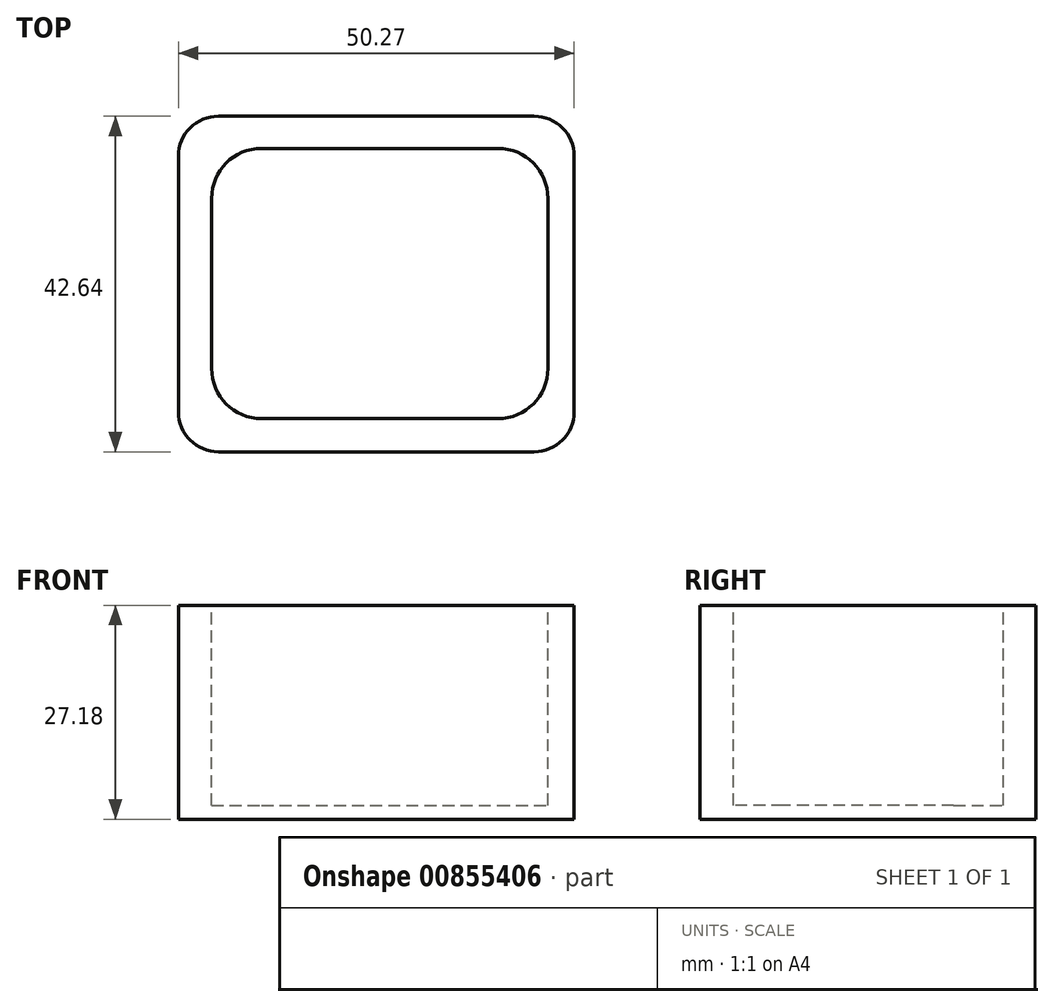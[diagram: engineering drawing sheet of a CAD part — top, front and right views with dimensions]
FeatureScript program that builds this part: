
annotation { "Feature Type Name" : "Feature", "Feature Type Description" : "" }
export const myFeature = defineFeature(function(context is Context, id is Id, definition is map)
    precondition{}
    {
        {
            var Q0;
            Q0=qCreatedBy(makeId("Top.planeOp"),FACE);
            var sketch = newSketch(context, id + "F0", { "sketchPlane" : qUnion([Q0])});
            skLineSegment(sketch, "E0.bottom", {"start": v(-56.09, -24.44) * mm, "end": v(-5.82, -24.44) * mm});
            skLineSegment(sketch, "E0.top", {"start": v(-56.09, -67.08) * mm, "end": v(-5.82, -67.08) * mm});
            skLineSegment(sketch, "E0.left", {"start": v(-56.09, -24.44) * mm, "end": v(-56.09, -67.08) * mm});
            skLineSegment(sketch, "E0.right", {"start": v(-5.82, -24.44) * mm, "end": v(-5.82, -67.08) * mm});
            skSolve(sketch);
        }
        {
            var Q0;
            Q0=makeQuery(id+"F0.imprint","IMPRINT",FACE,{"disambiguationData":[TD([[makeQuery(id+"F0.imprint","IMPRINT",EDGE,{"derivedFrom":sQuery(id+"F0.wireOp",EDGE,"E0.bottom")}),-1.0]])]});
            extrude(context, id + "F1", {"entities" : qUnion([Q0]), "depth" : 27.18 * mm, "offsetDistance" : 25.4 * mm});
        }
        {
            var Q0;
            Q0=makeQuery(id+"F1.opExtrude","CAP_FACE",FACE,{"disambiguationData":[OSD([sQuery(id+"F0.wireOp",EDGE,"E0.bottom"),sQuery(id+"F0.wireOp",EDGE,"E0.top"),sQuery(id+"F0.wireOp",EDGE,"E0.left"),sQuery(id+"F0.wireOp",EDGE,"E0.right")])],"isStart":false});
            var sketch = newSketch(context, id + "F2", { "sketchPlane" : qUnion([Q0])});
            skLineSegment(sketch, "E1.bottom", {"start": v(-45.52, -28.53) * mm, "end": v(-15.5, -28.53) * mm});
            skLineSegment(sketch, "E1.top", {"start": v(-45.52, -62.85) * mm, "end": v(-15.5, -62.85) * mm});
            skLineSegment(sketch, "E1.left", {"start": v(-51.87, -34.88) * mm, "end": v(-51.87, -56.5) * mm});
            skLineSegment(sketch, "E1.right", {"start": v(-9.15, -34.88) * mm, "end": v(-9.15, -56.5) * mm});
            skPoint(sketch, "E2.visualSharp", {"position": v(-51.87, -28.53) * mm});
            skArc(sketch, "E2.filletArc", {"start": v(-45.52, -28.53) * mm, "mid": v(-50.01, -30.39) * mm, "end": v(-51.87, -34.88) * mm});
            skPoint(sketch, "E3.visualSharp", {"position": v(-51.87, -62.85) * mm});
            skArc(sketch, "E3.filletArc", {"start": v(-51.87, -56.5) * mm, "mid": v(-50.01, -61) * mm, "end": v(-45.52, -62.85) * mm});
            skPoint(sketch, "E4.visualSharp", {"position": v(-9.15, -62.85) * mm});
            skArc(sketch, "E4.filletArc", {"start": v(-15.5, -62.85) * mm, "mid": v(-11.01, -61) * mm, "end": v(-9.15, -56.5) * mm});
            skPoint(sketch, "E5.visualSharp", {"position": v(-9.15, -28.53) * mm});
            skArc(sketch, "E5.filletArc", {"start": v(-9.15, -34.88) * mm, "mid": v(-11.01, -30.39) * mm, "end": v(-15.5, -28.53) * mm});
            skSolve(sketch);
        }
        {
            var Q0;
            Q0=makeQuery(id+"F2.imprint","IMPRINT",FACE,{"disambiguationData":[TD([[makeQuery(id+"F2.imprint","IMPRINT",EDGE,{"derivedFrom":sQuery(id+"F2.wireOp",EDGE,"E1.bottom")}),-1.0]])]});
            extrude(context, id + "F3", {"entities" : qUnion([Q0]), "operationType" : NewBodyOperationType.REMOVE, "oppositeDirection" : true, "depth" : 25.4 * mm, "offsetDistance" : 25.4 * mm});
        }
        {
            var Q0;
            Q0=makeQuery(id+"F1.opExtrude","SWEPT_EDGE",EDGE,{"disambiguationData":[OSD([sQuery(id+"F0.wireOp",EDGE,"E0.top"),sQuery(id+"F0.wireOp",EDGE,"E0.left")])]});
            fillet(context, id + "F4", {"entities" : qUnion([Q0]), "radius" : 5.08 * mm, "tangentPropagation" : true, "allowEdgeOverflow" : false});
        }
        {
            var Q0;
            Q0=makeQuery(id+"F1.opExtrude","SWEPT_EDGE",EDGE,{"disambiguationData":[OSD([sQuery(id+"F0.wireOp",EDGE,"E0.top"),sQuery(id+"F0.wireOp",EDGE,"E0.right")])]});
            fillet(context, id + "F5", {"entities" : qUnion([Q0]), "radius" : 5.08 * mm, "tangentPropagation" : true, "allowEdgeOverflow" : false});
        }
        {
            var Q0;
            Q0=makeQuery(id+"F1.opExtrude","SWEPT_EDGE",EDGE,{"disambiguationData":[OSD([sQuery(id+"F0.wireOp",EDGE,"E0.bottom"),sQuery(id+"F0.wireOp",EDGE,"E0.left")])]});
            fillet(context, id + "F6", {"entities" : qUnion([Q0]), "radius" : 5.08 * mm, "tangentPropagation" : true, "allowEdgeOverflow" : false});
        }
        {
            var Q0;
            Q0=makeQuery(id+"F1.opExtrude","SWEPT_EDGE",EDGE,{"disambiguationData":[OSD([sQuery(id+"F0.wireOp",EDGE,"E0.bottom"),sQuery(id+"F0.wireOp",EDGE,"E0.right")])]});
            fillet(context, id + "F7", {"entities" : qUnion([Q0]), "radius" : 5.08 * mm, "tangentPropagation" : true, "allowEdgeOverflow" : false});
        }
    });
